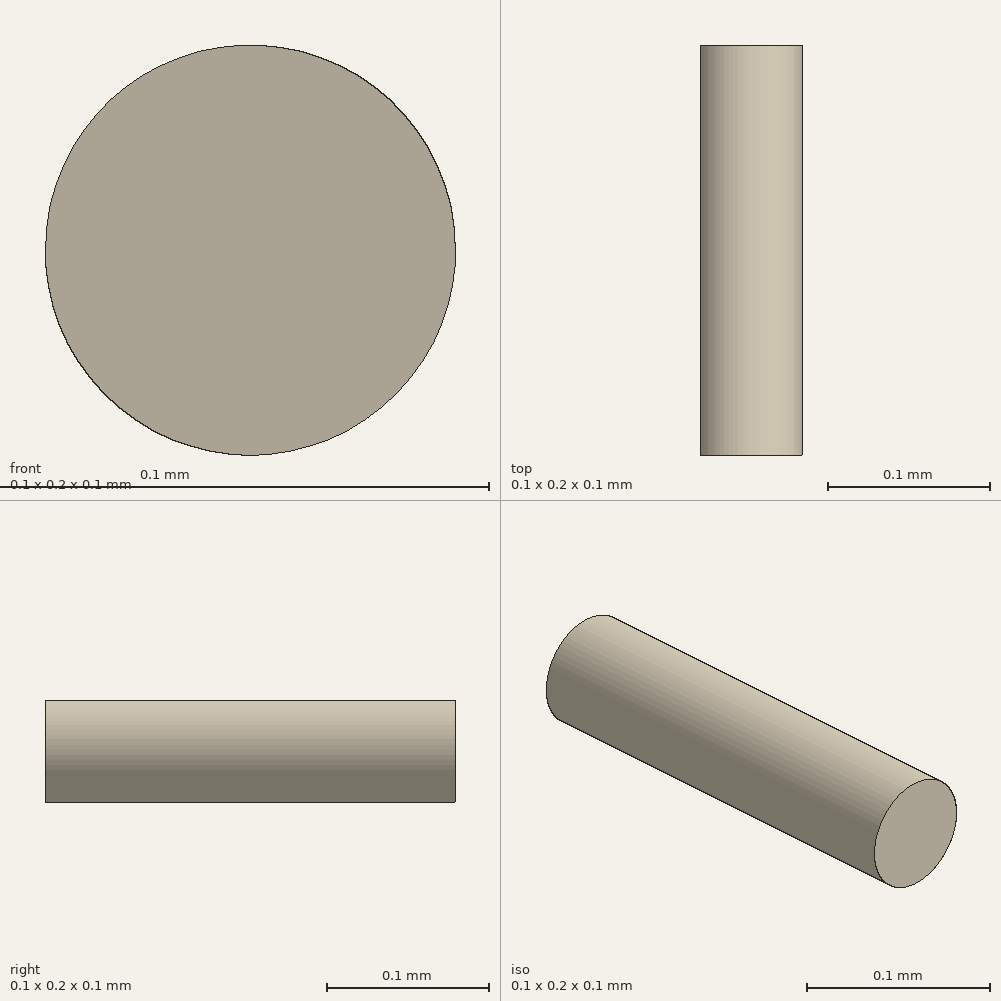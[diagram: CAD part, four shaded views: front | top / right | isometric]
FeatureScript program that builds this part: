
annotation { "Feature Type Name" : "Feature", "Feature Type Description" : "" }
export const myFeature = defineFeature(function(context is Context, id is Id, definition is map)
    precondition{}
    {
        {
            var Q0;
            Q0=qCreatedBy(makeId("Front.planeOp"),FACE);
            var sketch = newSketch(context, id + "F0", { "sketchPlane" : qUnion([Q0])});
            skCircle(sketch, "E0", {"center": v(0, 0) * mm, "radius": 0.03 * mm});
            skSolve(sketch);
        }
        {
            var Q0;
            Q0 = qSketchRegion(id + "F0", true);
            extrude(context, id + "F1", {"entities" : qUnion([Q0]), "depth" : 0.25 * mm, "offsetDistance" : 25.4 * mm});
        }
    });
